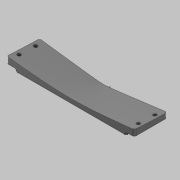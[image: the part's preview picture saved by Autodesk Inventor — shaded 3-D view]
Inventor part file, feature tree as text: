
AUTODESK INVENTOR PART (.ipt)
format: ipt  version: 2020 (Build 240168000, 168)  size: 7,950,336 bytes
history: native  units: in
note: dims shown in document units (in); Inventor stores cm internally (conversion verified against a paired STEP export)
features: sketch x19, extrude x14, plane x11, chamfer x8, other x6, fillet x4, revolve x3, split x3, hole x3, projected_geometry x2, sweep x1
ambient origin geometry x8: Origin, YZ Plane, XZ Plane, XY Plane, X Axis, Y Axis, Z Axis, Center Point
bodies: Solid7 (feature_tree), Solid8 (feature_tree), Solid10 (feature_tree)
feature tree (74):
  other  "ProfileTop"
  other  "ProfileSide"
  other  "XY_Project"
  other  "ProfileBack"
  revolve  "RevolvePlane"  [1 undecoded]
  revolve  "RevolveSketch"  [1 undecoded]
  extrude  "Extrusion5"  Depth=7.874in
  extrude  "Extrusion6"  Depth=5.4528in
  split  "Split1"
  revolve  "Revolution1"  [1 undecoded]
  chamfer  "Chamfer4"  [1 undecoded]
  chamfer  "Chamfer5"  Distance=0.5906in
  chamfer  "Chamfer6"  Distance=0.1969in
  chamfer  "Chamfer7"  Distance=0.1969in
  sweep  "Sweep1"
  chamfer  "Chamfer8"  Distance=8.1496in
  chamfer  "Chamfer9"  Distance=1.2598in
  chamfer  "Chamfer10"  Distance=10.9449in
  other  "SensorDivet"
  extrude  "Extrusion7"  Depth=0.1969in
  plane  "Work Plane6"
  plane  "Work Plane8"
  sketch  "Sketch12"  dims[d112=30.973in d142=7.874in]
  extrude  "BackSupport"  Depth=0.1969in
  extrude  "FrontSupport"  Depth=0.1969in
  plane  "Work Plane9"
  sketch  "Sketch19"  dims[d159=2.937in d160=16.7023in]
  sketch  "Sketch21"  dims[d161=16.7023in]
  extrude  "BaseVerticalExtend"  Depth=0.1969in
  plane  "Work Plane10"
  extrude  "BasePlate"  Depth=0.1969in
  extrude  "TriRib"  Depth=0.1969in TaperAngle=0.0deg
  extrude  "Slot"  Depth=0.1969in TaperAngle=0.0deg
  plane  "Work Plane11"
  extrude  "Extrusion19"  TaperAngle=180.0deg  [1 undecoded]
  extrude  "Extrusion20"  Depth=0.1969in
  hole  "Hole2"  [1 undecoded]
  fillet  "Fillet1"  Radius=5.4724in
  fillet  "Fillet2"  Radius=0.1969in
  fillet  "Fillet3"  Radius=0.1969in
  plane  "Work Plane13"
  split  "Split7"
  split  "Split8"
  plane  "Work Plane15"
  hole  "Hole3"  [1 undecoded]
  plane  "Work Plane16"
  hole  "Hole4"  [1 undecoded]
  chamfer  "Chamfer11"  [1 undecoded]
  plane  "Work Plane21"
  extrude  "Extrusion21"  Depth=0.1969in TaperAngle=45.0deg
  plane  "Work Plane22"
  extrude  "Extrusion22"  Depth=0.1969in TaperAngle=45.0deg
  sketch  "Sketch36"  dims[d179=1.6341in]
  plane  "Work Plane23"
  extrude  "Extrusion23"  Depth=0.1969in TaperAngle=45.0deg
  fillet  "Fillet4"  [1 undecoded]
  other  "Image8"
  sketch  "Sketch9"  dims[d98=7.874in d109=2.278in]
  sketch  "3D Sketch1"
  sketch  "Sketch10"  dims[d110=12.4228in d111=3.715in]
  sketch  "Sketch13"  dims[d155=5.4528in d158=5.4528in]
  projected_geometry  "Projected Loop1"
  projected_geometry  "Projected Loop2"
  sketch  "Sketch22"  dims[d162=2.937in]
  sketch  "Sketch23"  dims[d170=1.8504in]
  sketch  "Sketch24"  dims[d171=7.4452in]
  sketch  "Sketch26"  dims[d172=5.4724in]
  sketch  "Sketch27"  dims[d173=0.0in]
  sketch  "Sketch29"  dims[d174=4.9332in]
  sketch  "Sketch32"  dims[d175=5.4231in]
  sketch  "Sketch33"  dims[d176=1.7487in]
  sketch  "Sketch34"  dims[d177=4.8557in]
  sketch  "Sketch35"  dims[d178=1.8083in]
  sketch  "Sketch37"  dims[d180=0.8398in d181=0.0in d187=0.5906in d188=0.1969in d189=0.1969in d272=29.8893in d278=8.1496in d279=1.2598in d280=10.9449in d281=6.8898in d282=1.2598in d283=5.4724in d284=5.4724in d285=8.1496in d288=15.748in d289=0.0in d290=15.748in d291=0.0in d346=180.0deg d347=1.4961in d348=1.4961in d349=5.4724in d350=0.1969in d351=1.4961in d352=45.0deg d353=0.1969in d354=1.4961in d355=45.0deg d356=0.1969in d357=1.4961in d358=45.0deg d359=0.1969in d360=1.4961in d361=45.0deg d362=0.0in d363=0.0in d364=0.1969in d365=1.4961in d366=45.0deg d367=0.1969in d368=1.4961in d369=45.0deg d370=0.0591in d371=1.4961in d372=45.0deg d373=-1.9685in d375=0.0in d376=0.0in d377=1.4961in d378=1.4961in d379=0.0in d380=0.6693in d381=0.6693in d382=0.6693in d383=0.6693in d384=0.6693in d385=0.6693in d386=0.5512in d387=0.9055in d388=0.0in d397=-1.9685in d424=0.3937in d425=0.0in d426=1.9685in d427=0.0in d428=12.2047in d429=3.1496in d430=6.1024in d431=0.5906in d432=12.2047in d433=6.1024in d434=1.5748in d457=0.3937in d458=0.0in d459=0.0in d460=0.5906in d461=0.0in d462=3.1496in d463=3.1496in d464=0.7874in d465=0.7874in d466=4.9213in d467=4.9213in d468=0.1969in d469=0.1969in d470=3.937in d471=0.0in d479=0.4094in d480=0.7953in d481=0.0in d482=4.2126in d483=4.2126in d484=8.6693in d485=0.0in d490=-2.3622in d491=0.7874in d492=0.7874in d493=1.1811in d494=0.0in d495=0.7874in d496=0.7874in d497=0.7874in d498=0.0in d512=0.3937in d513=0.3937in d514=0.3937in d515=0.3937in d516=0.7874in d517=0.7874in d518=0.7874in d519=0.7874in d520=0.3937in d521=0.3937in d522=0.7874in d523=0.7874in d524=0.3307in d525=0.2362in d526=0.5669in d527=0.2756in d528=90.0deg d529=2.3622in d530=0.8108in d532=0.1969in d533=0.1575in d534=0.1575in d535=1.1811in d541=1.3061in d542=3.2283in d543=3.2283in d544=0.3307in d545=0.2362in d546=0.5512in d547=0.2756in d548=90.0deg d549=2.3622in d550=0.8108in d551=0.3937in d552=0.3937in d553=0.9936in d554=3.2283in d555=3.2283in d556=0.3937in d557=0.3937in d558=0.3307in d559=0.2362in d560=0.5512in d561=0.2756in d562=90.0deg d563=2.3622in d564=0.8108in d565=1.9685in d572=0.0394in d573=0.0787in d574=45.0deg d575=4.625in d576=0.0in d577=0.0in d578=0.4375in d579=0.0in d580=0.0in d581=-0.3125in d582=0.3937in d583=0.0in d584=0.1969in d163=0.0197in d164=0.0344in d165=0.0197in d166=0.0344in d440=0.0197in d441=0.0344in d442=0.0197in d443=0.0344in d449=0.0197in d450=0.0344in d451=0.0197in d452=0.0344in d540=0.0394in]
note: 10 required parameter values undecoded (feature->parameter linkage not recoverable at this tier; creation-order binding heuristic only, values carry confidence <= 0.55)